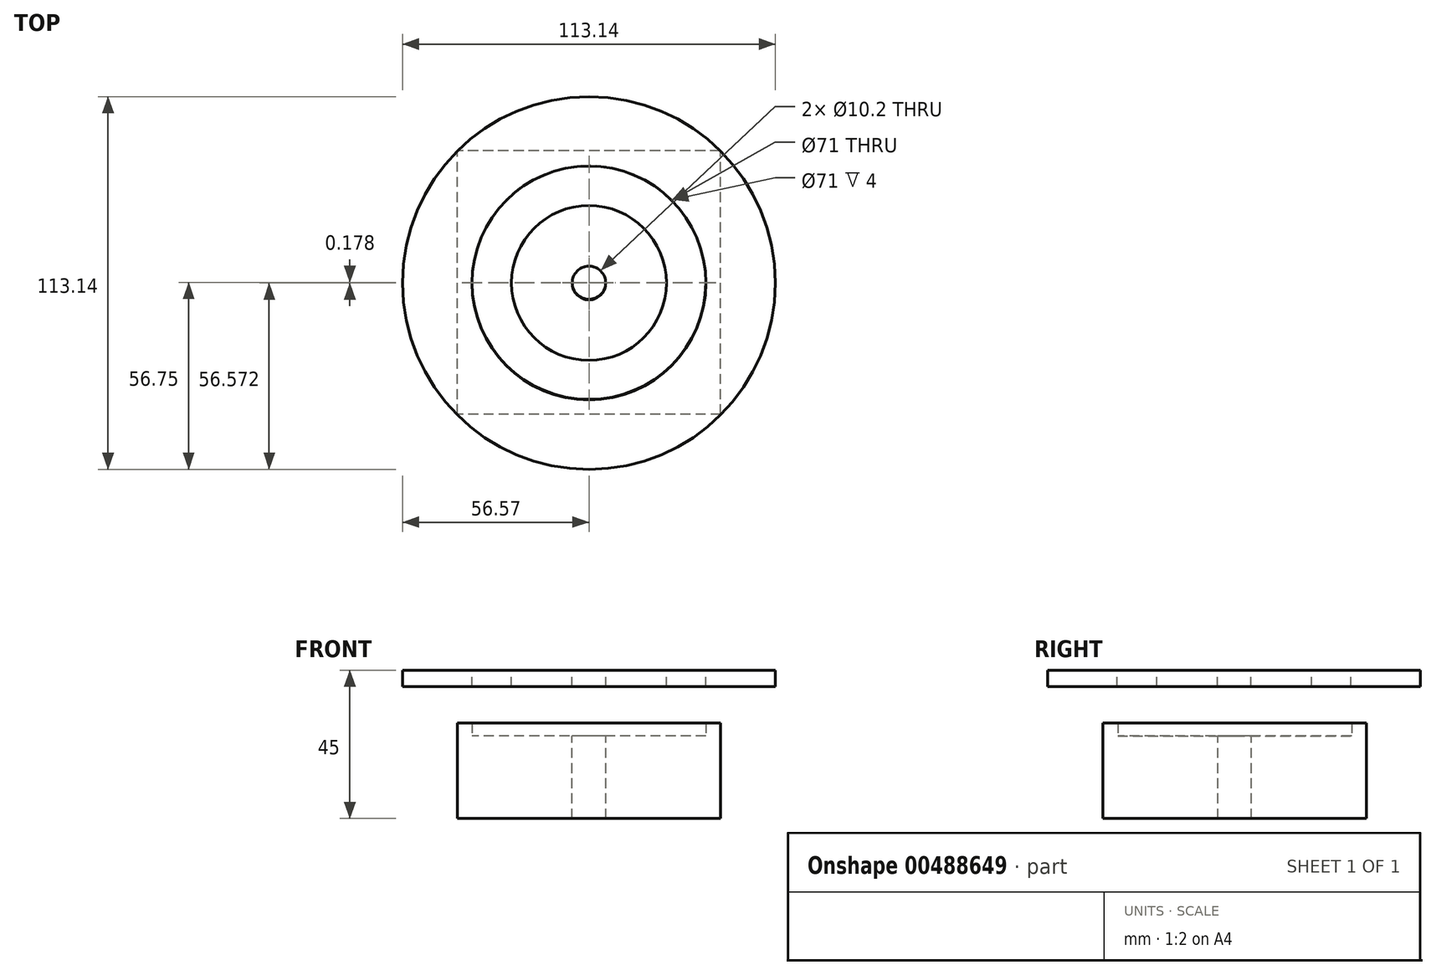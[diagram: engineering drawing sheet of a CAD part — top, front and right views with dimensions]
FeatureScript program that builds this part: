
annotation { "Feature Type Name" : "Feature", "Feature Type Description" : "" }
export const myFeature = defineFeature(function(context is Context, id is Id, definition is map)
    precondition{}
    {
        {
            var Q0;
            Q0=qCreatedBy(makeId("Top.planeOp"),FACE);
            var sketch = newSketch(context, id + "F0", { "sketchPlane" : qUnion([Q0])});
            skLineSegment(sketch, "E0.bottom", {"start": v(40, -40) * mm, "end": v(-40, -40) * mm});
            skLineSegment(sketch, "E0.top", {"start": v(40, 40) * mm, "end": v(-40, 40) * mm});
            skLineSegment(sketch, "E0.left", {"start": v(40, -40) * mm, "end": v(40, 40) * mm});
            skLineSegment(sketch, "E0.right", {"start": v(-40, -40) * mm, "end": v(-40, 40) * mm});
            skPoint(sketch, "E0.middle", {"position": v(0, 0) * mm});
            skCircle(sketch, "E1", {"center": v(0, 0) * mm, "radius": 35.5 * mm});
            skCircle(sketch, "E2", {"center": v(0, 0) * mm, "radius": 5.1 * mm});
            skSolve(sketch);
        }
        {
            var Q0;
            Q0=makeQuery(id+"F0.imprint","IMPRINT",FACE,{"disambiguationData":[TD([[makeQuery(id+"F0.imprint","IMPRINT",EDGE,{"derivedFrom":sQuery(id+"F0.wireOp",EDGE,"E0.bottom")}),-1.0]])]});
            extrude(context, id + "F1", {"entities" : qUnion([Q0]), "depth" : 4 * mm, "offsetDistance" : 25 * mm});
        }
        {
            var Q0;
            Q0=makeQuery(id+"F0.imprint","IMPRINT",FACE,{"disambiguationData":[TD([[makeQuery(id+"F0.imprint","IMPRINT",EDGE,{"derivedFrom":sQuery(id+"F0.wireOp",EDGE,"E0.bottom")}),-1.0]])]});
            var Q1;
            Q1=makeQuery(id+"F0.imprint","IMPRINT",FACE,{"disambiguationData":[TD([[makeQuery(id+"F0.imprint","IMPRINT",EDGE,{"derivedFrom":sQuery(id+"F0.wireOp",EDGE,"E1")}),1.0]])]});
            extrude(context, id + "F2", {"entities" : qUnion([Q0, Q1]), "operationType" : NewBodyOperationType.ADD, "oppositeDirection" : true, "depth" : 25 * mm, "offsetDistance" : 25 * mm});
        }
        {
            var Q0;
            Q0=qCreatedBy(makeId("Top.planeOp"),FACE);
            cPlane(context, id + "F3", {"entities" : qUnion([Q0]), "cplaneType" : CPlaneType.OFFSET, "offset" : 20 * mm, "width" : 150 * mm, "height" : 150 * mm});
        }
        {
            var Q0;
            Q0=qCreatedBy(id+"F3.planeOp",FACE);
            var Q1;
            Q1=qCreatedBy(id+"F3.planeOp",FACE);
            var sketch = newSketch(context, id + "F4", { "sketchPlane" : qUnion([Q0, Q1])});
            skPoint(sketch, "E3.middle", {"position": v(0, -0.18) * mm});
            skCircle(sketch, "E4", {"center": v(0, -0.18) * mm, "radius": 35.5 * mm});
            skCircle(sketch, "E5", {"center": v(0, -0.18) * mm, "radius": 23.5 * mm});
            skCircle(sketch, "E6", {"center": v(0, -0.18) * mm, "radius": 56.57 * mm});
            skCircle(sketch, "E7", {"center": v(0, -0.18) * mm, "radius": 5.1 * mm});
            skSolve(sketch);
        }
        {
            var Q0;
            Q0=makeQuery(id+"F4.imprint","IMPRINT",FACE,{"disambiguationData":[TD([[makeQuery(id+"F4.imprint","IMPRINT",EDGE,{"derivedFrom":sQuery(id+"F4.wireOp",EDGE,"E4")}),-1.0]])]});
            var Q1;
            Q1=makeQuery(id+"F4.imprint","IMPRINT",FACE,{"disambiguationData":[TD([[makeQuery(id+"F4.imprint","IMPRINT",EDGE,{"derivedFrom":sQuery(id+"F4.wireOp",EDGE,"E5")}),1.0]])]});
            extrude(context, id + "F5", {"entities" : qUnion([Q0, Q1]), "oppositeDirection" : true, "depth" : 5 * mm, "offsetDistance" : 25 * mm});
        }
    });
